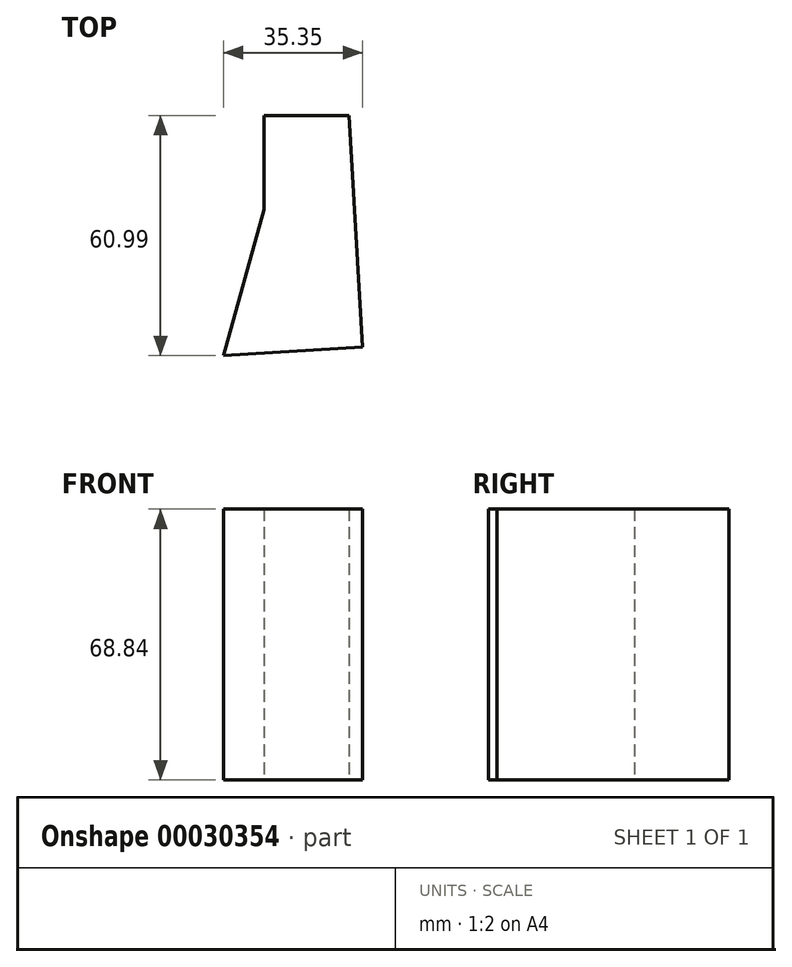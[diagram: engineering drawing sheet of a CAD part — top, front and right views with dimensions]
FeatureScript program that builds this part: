
annotation { "Feature Type Name" : "Feature", "Feature Type Description" : "" }
export const myFeature = defineFeature(function(context is Context, id is Id, definition is map)
    precondition{}
    {
        {
            var Q0;
            Q0=qCreatedBy(makeId("Top.planeOp"),FACE);
            var sketch = newSketch(context, id + "F0", { "sketchPlane" : qUnion([Q0])});
            skLineSegment(sketch, "E0", {"start": v(-25.07, 34.92) * mm, "end": v(-25.07, 58.87) * mm});
            skLineSegment(sketch, "E1", {"start": v(-25.07, 58.87) * mm, "end": v(-3.53, 58.87) * mm});
            skLineSegment(sketch, "E2", {"start": v(-3.53, 58.87) * mm, "end": v(0, 0) * mm});
            skLineSegment(sketch, "E3", {"start": v(0, 0) * mm, "end": v(-35.35, -2.12) * mm});
            skLineSegment(sketch, "E4", {"start": v(-35.35, -2.12) * mm, "end": v(-25.07, 34.92) * mm});
            skSolve(sketch);
        }
        {
            var Q0;
            Q0 = qSketchRegion(id + "F0", true);
            extrude(context, id + "F1", {"entities" : qUnion([Q0]), "depth" : 68.84 * mm});
        }
    });
